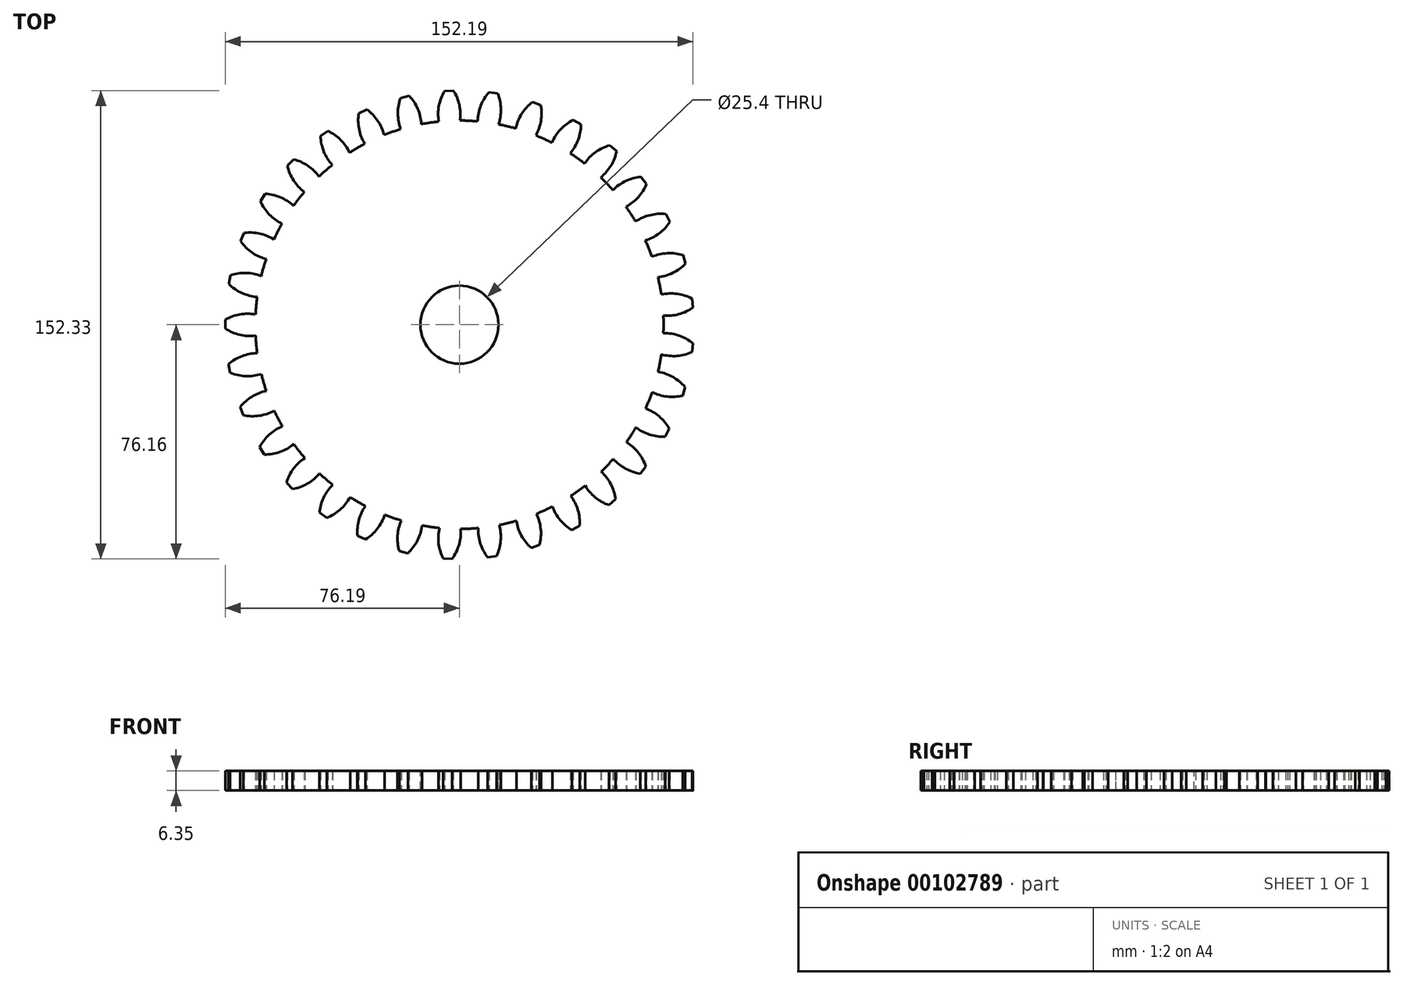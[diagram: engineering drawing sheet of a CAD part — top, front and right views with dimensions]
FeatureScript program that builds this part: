
annotation { "Feature Type Name" : "Feature", "Feature Type Description" : "" }
export const myFeature = defineFeature(function(context is Context, id is Id, definition is map)
    precondition{}
    {
        {
            var Q0;
            Q0=qCreatedBy(makeId("Top.planeOp"),FACE);
            var sketch = newSketch(context, id + "F0", { "sketchPlane" : qUnion([Q0])});
            skCircle(sketch, "E0", {"center": v(0, 0) * mm, "radius": 66.42 * mm});
            skCircle(sketch, "E1", {"center": v(0, 0) * mm, "radius": 71.37 * mm, "construction": true});
            skCircle(sketch, "E2", {"center": v(0, 0) * mm, "radius": 76.2 * mm, "construction": true});
            skLineSegment(sketch, "E3", {"start": v(0, 0) * mm, "end": v(-4.85, 101.64) * mm, "construction": true});
            skLineSegment(sketch, "E4", {"start": v(0, 0) * mm, "end": v(0, 101.64) * mm, "construction": true});
            skLineSegment(sketch, "E5", {"start": v(0, 71.37) * mm, "end": v(-102.05, 49.76) * mm, "construction": true});
            skLineSegment(sketch, "E6", {"start": v(0, 71.37) * mm, "end": v(-103.29, 85.97) * mm, "construction": true});
            skCircle(sketch, "E7", {"center": v(0, 71.37) * mm, "radius": 14.6 * mm, "construction": true});
            skArc(sketch, "E8", {"start": v(-1.96, 76.17) * mm, "mid": v(-28.55, 65.2) * mm, "end": v(0.19, 66.42) * mm, "construction": true});
            skArc(sketch, "E9", {"start": v(0.19, 66.42) * mm, "mid": v(-0.02, 71.49) * mm, "end": v(-1.96, 76.17) * mm});
            skArc(sketch, "E10", {"start": v(-4.84, 76.05) * mm, "mid": v(-6.67, 71.23) * mm, "end": v(-6.7, 66.08) * mm});
            skLineSegment(sketch, "E11", {"start": v(-4.84, 76.05) * mm, "end": v(-1.96, 76.17) * mm});
            skLineSegment(sketch, "E12.1.0", {"start": v(-19.15, 73.76) * mm, "end": v(-16.34, 74.43) * mm});
            skArc(sketch, "E12.1.1", {"start": v(-19.15, 73.76) * mm, "mid": v(-20.03, 68.68) * mm, "end": v(-19.1, 63.62) * mm});
            skArc(sketch, "E12.1.2", {"start": v(-12.38, 65.26) * mm, "mid": v(-13.55, 70.2) * mm, "end": v(-16.34, 74.43) * mm});
            skLineSegment(sketch, "E12.2.0", {"start": v(-32.76, 68.8) * mm, "end": v(-30.13, 70) * mm});
            skArc(sketch, "E12.2.1", {"start": v(-32.76, 68.8) * mm, "mid": v(-32.66, 63.65) * mm, "end": v(-30.79, 58.86) * mm});
            skArc(sketch, "E12.2.2", {"start": v(-24.51, 61.73) * mm, "mid": v(-26.6, 66.36) * mm, "end": v(-30.13, 70) * mm});
            skLineSegment(sketch, "E12.3.0", {"start": v(-45.19, 61.36) * mm, "end": v(-42.83, 63.02) * mm});
            skArc(sketch, "E12.3.1", {"start": v(-45.19, 61.36) * mm, "mid": v(-44.12, 56.32) * mm, "end": v(-41.37, 51.97) * mm});
            skArc(sketch, "E12.3.2", {"start": v(-35.75, 55.98) * mm, "mid": v(-38.67, 60.13) * mm, "end": v(-42.83, 63.02) * mm});
            skLineSegment(sketch, "E12.4.0", {"start": v(-55.98, 51.7) * mm, "end": v(-53.98, 53.78) * mm});
            skArc(sketch, "E12.4.1", {"start": v(-55.98, 51.7) * mm, "mid": v(-53.98, 46.95) * mm, "end": v(-50.45, 43.2) * mm});
            skArc(sketch, "E12.4.2", {"start": v(-45.7, 48.2) * mm, "mid": v(-49.35, 51.72) * mm, "end": v(-53.98, 53.78) * mm});
            skLineSegment(sketch, "E12.5.0", {"start": v(-64.75, 40.17) * mm, "end": v(-63.19, 42.6) * mm});
            skArc(sketch, "E12.5.1", {"start": v(-64.75, 40.17) * mm, "mid": v(-61.89, 35.89) * mm, "end": v(-57.72, 32.87) * mm});
            skArc(sketch, "E12.5.2", {"start": v(-54, 38.68) * mm, "mid": v(-58.25, 41.45) * mm, "end": v(-63.19, 42.6) * mm});
            skLineSegment(sketch, "E12.6.0", {"start": v(-71.19, 27.19) * mm, "end": v(-70.1, 29.86) * mm});
            skArc(sketch, "E12.6.1", {"start": v(-71.19, 27.19) * mm, "mid": v(-67.56, 23.53) * mm, "end": v(-62.9, 21.35) * mm});
            skArc(sketch, "E12.6.2", {"start": v(-60.34, 27.76) * mm, "mid": v(-65.04, 29.67) * mm, "end": v(-70.1, 29.86) * mm});
            skLineSegment(sketch, "E12.7.0", {"start": v(-75.04, 13.22) * mm, "end": v(-74.49, 16.06) * mm});
            skArc(sketch, "E12.7.1", {"start": v(-75.04, 13.22) * mm, "mid": v(-70.8, 10.31) * mm, "end": v(-65.8, 9.06) * mm});
            skArc(sketch, "E12.7.2", {"start": v(-64.5, 15.84) * mm, "mid": v(-69.48, 16.83) * mm, "end": v(-74.49, 16.06) * mm});
            skLineSegment(sketch, "E12.8.0", {"start": v(-76.2, -1.22) * mm, "end": v(-76.18, 1.67) * mm});
            skArc(sketch, "E12.8.1", {"start": v(-76.2, -1.22) * mm, "mid": v(-71.47, -3.27) * mm, "end": v(-66.33, -3.55) * mm});
            skArc(sketch, "E12.8.2", {"start": v(-66.34, 3.35) * mm, "mid": v(-71.4, 3.38) * mm, "end": v(-76.18, 1.67) * mm});
            skLineSegment(sketch, "E12.9.0", {"start": v(-74.58, -15.62) * mm, "end": v(-75.12, -12.78) * mm});
            skArc(sketch, "E12.9.1", {"start": v(-74.58, -15.62) * mm, "mid": v(-69.56, -16.74) * mm, "end": v(-64.45, -16.04) * mm});
            skArc(sketch, "E12.9.2", {"start": v(-65.77, -9.27) * mm, "mid": v(-70.76, -10.2) * mm, "end": v(-75.12, -12.78) * mm});
            skLineSegment(sketch, "E12.10.0", {"start": v(-70.28, -29.45) * mm, "end": v(-71.35, -26.76) * mm});
            skArc(sketch, "E12.10.1", {"start": v(-70.28, -29.45) * mm, "mid": v(-65.13, -29.6) * mm, "end": v(-60.25, -27.95) * mm});
            skArc(sketch, "E12.10.2", {"start": v(-62.83, -21.55) * mm, "mid": v(-67.55, -23.4) * mm, "end": v(-71.35, -26.76) * mm});
            skLineSegment(sketch, "E12.11.0", {"start": v(-63.44, -42.22) * mm, "end": v(-65, -39.78) * mm});
            skArc(sketch, "E12.11.1", {"start": v(-63.44, -42.22) * mm, "mid": v(-58.35, -41.39) * mm, "end": v(-53.88, -38.85) * mm});
            skArc(sketch, "E12.11.2", {"start": v(-57.62, -33.05) * mm, "mid": v(-61.9, -35.76) * mm, "end": v(-65, -39.78) * mm});
            skLineSegment(sketch, "E12.12.0", {"start": v(-54.3, -53.46) * mm, "end": v(-56.29, -51.36) * mm});
            skArc(sketch, "E12.12.1", {"start": v(-54.3, -53.46) * mm, "mid": v(-49.47, -51.68) * mm, "end": v(-45.55, -48.34) * mm});
            skArc(sketch, "E12.12.2", {"start": v(-50.32, -43.35) * mm, "mid": v(-54.01, -46.83) * mm, "end": v(-56.29, -51.36) * mm});
            skLineSegment(sketch, "E12.13.0", {"start": v(-43.2, -62.77) * mm, "end": v(-45.55, -61.09) * mm});
            skArc(sketch, "E12.13.1", {"start": v(-43.2, -62.77) * mm, "mid": v(-38.8, -60.11) * mm, "end": v(-35.58, -56.09) * mm});
            skArc(sketch, "E12.13.2", {"start": v(-41.2, -52.1) * mm, "mid": v(-44.17, -56.2) * mm, "end": v(-45.55, -61.09) * mm});
            skLineSegment(sketch, "E12.14.0", {"start": v(-30.54, -69.81) * mm, "end": v(-33.17, -68.6) * mm});
            skArc(sketch, "E12.14.1", {"start": v(-30.54, -69.81) * mm, "mid": v(-26.71, -66.37) * mm, "end": v(-24.32, -61.8) * mm});
            skArc(sketch, "E12.14.2", {"start": v(-30.6, -58.95) * mm, "mid": v(-32.74, -63.55) * mm, "end": v(-33.17, -68.6) * mm});
            skLineSegment(sketch, "E12.15.0", {"start": v(-16.78, -74.33) * mm, "end": v(-19.58, -73.64) * mm});
            skArc(sketch, "E12.15.1", {"start": v(-16.78, -74.33) * mm, "mid": v(-13.67, -70.22) * mm, "end": v(-12.18, -65.3) * mm});
            skArc(sketch, "E12.15.2", {"start": v(-18.9, -63.68) * mm, "mid": v(-20.12, -68.6) * mm, "end": v(-19.58, -73.64) * mm});
            skLineSegment(sketch, "E12.16.0", {"start": v(-2.4, -76.16) * mm, "end": v(-5.3, -76.02) * mm});
            skArc(sketch, "E12.16.1", {"start": v(-2.4, -76.16) * mm, "mid": v(-0.13, -71.54) * mm, "end": v(0.4, -66.42) * mm});
            skArc(sketch, "E12.16.2", {"start": v(-6.5, -66.1) * mm, "mid": v(-6.77, -71.17) * mm, "end": v(-5.3, -76.02) * mm});
            skLineSegment(sketch, "E12.17.0", {"start": v(12.05, -75.24) * mm, "end": v(9.19, -75.64) * mm});
            skArc(sketch, "E12.17.1", {"start": v(12.05, -75.24) * mm, "mid": v(13.4, -70.27) * mm, "end": v(12.96, -65.14) * mm});
            skArc(sketch, "E12.17.2", {"start": v(6.13, -66.14) * mm, "mid": v(6.82, -71.16) * mm, "end": v(9.19, -75.64) * mm});
            skLineSegment(sketch, "E12.18.0", {"start": v(26.07, -71.6) * mm, "end": v(23.34, -72.54) * mm});
            skArc(sketch, "E12.18.1", {"start": v(26.07, -71.6) * mm, "mid": v(26.46, -66.47) * mm, "end": v(25.05, -61.52) * mm});
            skArc(sketch, "E12.18.2", {"start": v(18.53, -63.78) * mm, "mid": v(20.16, -68.58) * mm, "end": v(23.34, -72.54) * mm});
            skLineSegment(sketch, "E12.19.0", {"start": v(39.15, -65.37) * mm, "end": v(36.65, -66.8) * mm});
            skArc(sketch, "E12.19.1", {"start": v(39.15, -65.37) * mm, "mid": v(38.57, -60.26) * mm, "end": v(36.24, -55.66) * mm});
            skArc(sketch, "E12.19.2", {"start": v(30.27, -59.12) * mm, "mid": v(32.78, -63.53) * mm, "end": v(36.65, -66.8) * mm});
            skLineSegment(sketch, "E12.20.0", {"start": v(50.81, -56.78) * mm, "end": v(48.63, -58.67) * mm});
            skArc(sketch, "E12.20.1", {"start": v(50.81, -56.78) * mm, "mid": v(49.27, -51.87) * mm, "end": v(46.12, -47.8) * mm});
            skArc(sketch, "E12.20.2", {"start": v(40.9, -52.33) * mm, "mid": v(44.2, -56.18) * mm, "end": v(48.63, -58.67) * mm});
            skLineSegment(sketch, "E12.21.0", {"start": v(60.64, -46.14) * mm, "end": v(58.85, -48.4) * mm});
            skArc(sketch, "E12.21.1", {"start": v(60.64, -46.14) * mm, "mid": v(58.2, -41.6) * mm, "end": v(54.33, -38.2) * mm});
            skArc(sketch, "E12.21.2", {"start": v(50.07, -43.64) * mm, "mid": v(54.04, -46.8) * mm, "end": v(58.85, -48.4) * mm});
            skLineSegment(sketch, "E12.22.0", {"start": v(68.28, -33.83) * mm, "end": v(66.95, -36.4) * mm});
            skArc(sketch, "E12.22.1", {"start": v(68.28, -33.83) * mm, "mid": v(65.02, -29.84) * mm, "end": v(60.58, -27.23) * mm});
            skArc(sketch, "E12.22.2", {"start": v(57.43, -33.37) * mm, "mid": v(61.92, -35.72) * mm, "end": v(66.95, -36.4) * mm});
            skLineSegment(sketch, "E12.23.0", {"start": v(73.45, -20.3) * mm, "end": v(72.63, -23.06) * mm});
            skArc(sketch, "E12.23.1", {"start": v(73.45, -20.3) * mm, "mid": v(69.5, -17) * mm, "end": v(64.64, -15.28) * mm});
            skArc(sketch, "E12.23.2", {"start": v(62.7, -21.9) * mm, "mid": v(67.56, -23.36) * mm, "end": v(72.63, -23.06) * mm});
            skLineSegment(sketch, "E12.24.0", {"start": v(75.96, -6.03) * mm, "end": v(75.68, -8.9) * mm});
            skArc(sketch, "E12.24.1", {"start": v(75.96, -6.03) * mm, "mid": v(71.45, -3.54) * mm, "end": v(66.36, -2.77) * mm});
            skArc(sketch, "E12.24.2", {"start": v(65.72, -9.64) * mm, "mid": v(70.76, -10.15) * mm, "end": v(75.68, -8.9) * mm});
            skLineSegment(sketch, "E12.25.0", {"start": v(75.73, 8.46) * mm, "end": v(76, 5.58) * mm});
            skArc(sketch, "E12.25.1", {"start": v(75.73, 8.46) * mm, "mid": v(70.83, 10.05) * mm, "end": v(65.69, 9.84) * mm});
            skArc(sketch, "E12.25.2", {"start": v(66.35, 2.97) * mm, "mid": v(71.4, 3.43) * mm, "end": v(76, 5.58) * mm});
            skLineSegment(sketch, "E12.26.0", {"start": v(72.76, 22.63) * mm, "end": v(73.57, 19.86) * mm});
            skArc(sketch, "E12.26.1", {"start": v(72.76, 22.63) * mm, "mid": v(67.65, 23.27) * mm, "end": v(62.64, 22.1) * mm});
            skArc(sketch, "E12.26.2", {"start": v(64.6, 15.48) * mm, "mid": v(69.47, 16.88) * mm, "end": v(73.57, 19.86) * mm});
            skLineSegment(sketch, "E12.27.0", {"start": v(67.16, 36) * mm, "end": v(68.48, 33.42) * mm});
            skArc(sketch, "E12.27.1", {"start": v(67.16, 36) * mm, "mid": v(62.02, 35.65) * mm, "end": v(57.32, 33.55) * mm});
            skArc(sketch, "E12.27.2", {"start": v(60.5, 27.42) * mm, "mid": v(65.02, 29.72) * mm, "end": v(68.48, 33.42) * mm});
            skLineSegment(sketch, "E12.28.0", {"start": v(59.14, 48.06) * mm, "end": v(60.91, 45.78) * mm});
            skArc(sketch, "E12.28.1", {"start": v(59.14, 48.06) * mm, "mid": v(54.16, 46.75) * mm, "end": v(49.94, 43.8) * mm});
            skArc(sketch, "E12.28.2", {"start": v(54.21, 38.37) * mm, "mid": v(58.22, 41.49) * mm, "end": v(60.91, 45.78) * mm});
            skLineSegment(sketch, "E12.29.0", {"start": v(48.97, 58.38) * mm, "end": v(51.15, 56.48) * mm});
            skArc(sketch, "E12.29.1", {"start": v(48.97, 58.38) * mm, "mid": v(44.33, 56.15) * mm, "end": v(40.75, 52.45) * mm});
            skArc(sketch, "E12.29.2", {"start": v(45.97, 47.94) * mm, "mid": v(49.31, 51.75) * mm, "end": v(51.15, 56.48) * mm});
            skLineSegment(sketch, "E12.30.0", {"start": v(37.04, 66.6) * mm, "end": v(39.54, 65.14) * mm});
            skArc(sketch, "E12.30.1", {"start": v(37.04, 66.6) * mm, "mid": v(32.9, 63.53) * mm, "end": v(30.08, 59.22) * mm});
            skArc(sketch, "E12.30.2", {"start": v(36.07, 55.77) * mm, "mid": v(38.63, 60.15) * mm, "end": v(39.54, 65.14) * mm});
            skLineSegment(sketch, "E12.31.0", {"start": v(23.77, 72.4) * mm, "end": v(26.5, 71.45) * mm});
            skArc(sketch, "E12.31.1", {"start": v(23.77, 72.4) * mm, "mid": v(20.28, 68.6) * mm, "end": v(18.33, 63.84) * mm});
            skArc(sketch, "E12.31.2", {"start": v(24.86, 61.6) * mm, "mid": v(26.55, 66.38) * mm, "end": v(26.5, 71.45) * mm});
            skLineSegment(sketch, "E12.32.0", {"start": v(9.64, 75.59) * mm, "end": v(12.5, 75.17) * mm});
            skArc(sketch, "E12.32.1", {"start": v(9.64, 75.59) * mm, "mid": v(6.93, 71.2) * mm, "end": v(5.92, 66.16) * mm});
            skArc(sketch, "E12.32.2", {"start": v(12.76, 65.18) * mm, "mid": v(13.5, 70.2) * mm, "end": v(12.5, 75.17) * mm});
            skLineSegment(sketch, "E13", {"start": v(0.19, 66.42) * mm, "end": v(5.92, 66.16) * mm});
            skLineSegment(sketch, "E14", {"start": v(5.92, 66.16) * mm, "end": v(12.76, 65.18) * mm});
            skPoint(sketch, "E15", {"position": v(-3.63, 76.1) * mm});
            skPoint(sketch, "E16", {"position": v(11.07, 75.38) * mm});
            skPoint(sketch, "E17", {"position": v(6.87, 71.04) * mm});
            skPoint(sketch, "E18", {"position": v(-6.7, 71.06) * mm});
            skSolve(sketch);
        }
        {
            var Q0;
            Q0 = qSketchRegion(id + "F0", true);
            extrude(context, id + "F1", {"entities" : qUnion([Q0]), "depth" : 6.35 * mm});
        }
        {
            var Q0;
            Q0=makeQuery(id+"F1.opExtrude","CAP_FACE",FACE,{"disambiguationData":[OSD([sQuery(id+"F0.wireOp",EDGE,"E0"),sQuery(id+"F0.wireOp",EDGE,"E9"),sQuery(id+"F0.wireOp",EDGE,"E10"),sQuery(id+"F0.wireOp",EDGE,"E11"),sQuery(id+"F0.wireOp",EDGE,"E12.1.0"),sQuery(id+"F0.wireOp",EDGE,"E12.1.1"),sQuery(id+"F0.wireOp",EDGE,"E12.1.2"),sQuery(id+"F0.wireOp",EDGE,"E12.2.0"),sQuery(id+"F0.wireOp",EDGE,"E12.2.1"),sQuery(id+"F0.wireOp",EDGE,"E12.2.2"),sQuery(id+"F0.wireOp",EDGE,"E12.3.0"),sQuery(id+"F0.wireOp",EDGE,"E12.3.1"),sQuery(id+"F0.wireOp",EDGE,"E12.3.2"),sQuery(id+"F0.wireOp",EDGE,"E12.4.0"),sQuery(id+"F0.wireOp",EDGE,"E12.4.1"),sQuery(id+"F0.wireOp",EDGE,"E12.4.2"),sQuery(id+"F0.wireOp",EDGE,"E12.5.0"),sQuery(id+"F0.wireOp",EDGE,"E12.5.1"),sQuery(id+"F0.wireOp",EDGE,"E12.5.2"),sQuery(id+"F0.wireOp",EDGE,"E12.6.0"),sQuery(id+"F0.wireOp",EDGE,"E12.6.1"),sQuery(id+"F0.wireOp",EDGE,"E12.6.2"),sQuery(id+"F0.wireOp",EDGE,"E12.7.0"),sQuery(id+"F0.wireOp",EDGE,"E12.7.1"),sQuery(id+"F0.wireOp",EDGE,"E12.7.2"),sQuery(id+"F0.wireOp",EDGE,"E12.8.0"),sQuery(id+"F0.wireOp",EDGE,"E12.8.1"),sQuery(id+"F0.wireOp",EDGE,"E12.8.2"),sQuery(id+"F0.wireOp",EDGE,"E12.9.0"),sQuery(id+"F0.wireOp",EDGE,"E12.9.1"),sQuery(id+"F0.wireOp",EDGE,"E12.9.2"),sQuery(id+"F0.wireOp",EDGE,"E12.10.0"),sQuery(id+"F0.wireOp",EDGE,"E12.10.1"),sQuery(id+"F0.wireOp",EDGE,"E12.10.2"),sQuery(id+"F0.wireOp",EDGE,"E12.11.0"),sQuery(id+"F0.wireOp",EDGE,"E12.11.1"),sQuery(id+"F0.wireOp",EDGE,"E12.11.2"),sQuery(id+"F0.wireOp",EDGE,"E12.12.0"),sQuery(id+"F0.wireOp",EDGE,"E12.12.1"),sQuery(id+"F0.wireOp",EDGE,"E12.12.2"),sQuery(id+"F0.wireOp",EDGE,"E12.13.0"),sQuery(id+"F0.wireOp",EDGE,"E12.13.1"),sQuery(id+"F0.wireOp",EDGE,"E12.13.2"),sQuery(id+"F0.wireOp",EDGE,"E12.14.0"),sQuery(id+"F0.wireOp",EDGE,"E12.14.1"),sQuery(id+"F0.wireOp",EDGE,"E12.14.2"),sQuery(id+"F0.wireOp",EDGE,"E12.15.0"),sQuery(id+"F0.wireOp",EDGE,"E12.15.1"),sQuery(id+"F0.wireOp",EDGE,"E12.15.2"),sQuery(id+"F0.wireOp",EDGE,"E12.16.0"),sQuery(id+"F0.wireOp",EDGE,"E12.16.1"),sQuery(id+"F0.wireOp",EDGE,"E12.16.2"),sQuery(id+"F0.wireOp",EDGE,"E12.17.0"),sQuery(id+"F0.wireOp",EDGE,"E12.17.1"),sQuery(id+"F0.wireOp",EDGE,"E12.17.2"),sQuery(id+"F0.wireOp",EDGE,"E12.18.0"),sQuery(id+"F0.wireOp",EDGE,"E12.18.1"),sQuery(id+"F0.wireOp",EDGE,"E12.18.2"),sQuery(id+"F0.wireOp",EDGE,"E12.19.0"),sQuery(id+"F0.wireOp",EDGE,"E12.19.1"),sQuery(id+"F0.wireOp",EDGE,"E12.19.2"),sQuery(id+"F0.wireOp",EDGE,"E12.20.0"),sQuery(id+"F0.wireOp",EDGE,"E12.20.1"),sQuery(id+"F0.wireOp",EDGE,"E12.20.2"),sQuery(id+"F0.wireOp",EDGE,"E12.21.0"),sQuery(id+"F0.wireOp",EDGE,"E12.21.1"),sQuery(id+"F0.wireOp",EDGE,"E12.21.2"),sQuery(id+"F0.wireOp",EDGE,"E12.22.0"),sQuery(id+"F0.wireOp",EDGE,"E12.22.1"),sQuery(id+"F0.wireOp",EDGE,"E12.22.2"),sQuery(id+"F0.wireOp",EDGE,"E12.23.0"),sQuery(id+"F0.wireOp",EDGE,"E12.23.1"),sQuery(id+"F0.wireOp",EDGE,"E12.23.2"),sQuery(id+"F0.wireOp",EDGE,"E12.24.0"),sQuery(id+"F0.wireOp",EDGE,"E12.24.1"),sQuery(id+"F0.wireOp",EDGE,"E12.24.2"),sQuery(id+"F0.wireOp",EDGE,"E12.25.0"),sQuery(id+"F0.wireOp",EDGE,"E12.25.1"),sQuery(id+"F0.wireOp",EDGE,"E12.25.2"),sQuery(id+"F0.wireOp",EDGE,"E12.26.0"),sQuery(id+"F0.wireOp",EDGE,"E12.26.1"),sQuery(id+"F0.wireOp",EDGE,"E12.26.2"),sQuery(id+"F0.wireOp",EDGE,"E12.27.0"),sQuery(id+"F0.wireOp",EDGE,"E12.27.1"),sQuery(id+"F0.wireOp",EDGE,"E12.27.2"),sQuery(id+"F0.wireOp",EDGE,"E12.28.0"),sQuery(id+"F0.wireOp",EDGE,"E12.28.1"),sQuery(id+"F0.wireOp",EDGE,"E12.28.2"),sQuery(id+"F0.wireOp",EDGE,"E12.29.0"),sQuery(id+"F0.wireOp",EDGE,"E12.29.1"),sQuery(id+"F0.wireOp",EDGE,"E12.29.2"),sQuery(id+"F0.wireOp",EDGE,"E12.30.0"),sQuery(id+"F0.wireOp",EDGE,"E12.30.1"),sQuery(id+"F0.wireOp",EDGE,"E12.30.2"),sQuery(id+"F0.wireOp",EDGE,"E12.31.0"),sQuery(id+"F0.wireOp",EDGE,"E12.31.1"),sQuery(id+"F0.wireOp",EDGE,"E12.31.2"),sQuery(id+"F0.wireOp",EDGE,"E12.32.0"),sQuery(id+"F0.wireOp",EDGE,"E12.32.1"),sQuery(id+"F0.wireOp",EDGE,"E12.32.2")])],"isStart":false});
            var sketch = newSketch(context, id + "F2", { "sketchPlane" : qUnion([Q0])});
            skCircle(sketch, "E19", {"center": v(0, 0) * mm, "radius": 12.7 * mm});
            skSolve(sketch);
        }
        {
            var Q0;
            Q0 = qSketchRegion(id + "F2", true);
            extrude(context, id + "F3", {"entities" : qUnion([Q0]), "operationType" : NewBodyOperationType.REMOVE, "oppositeDirection" : true, "depth" : 25.4 * mm, "symmetric" : true});
        }
    });
